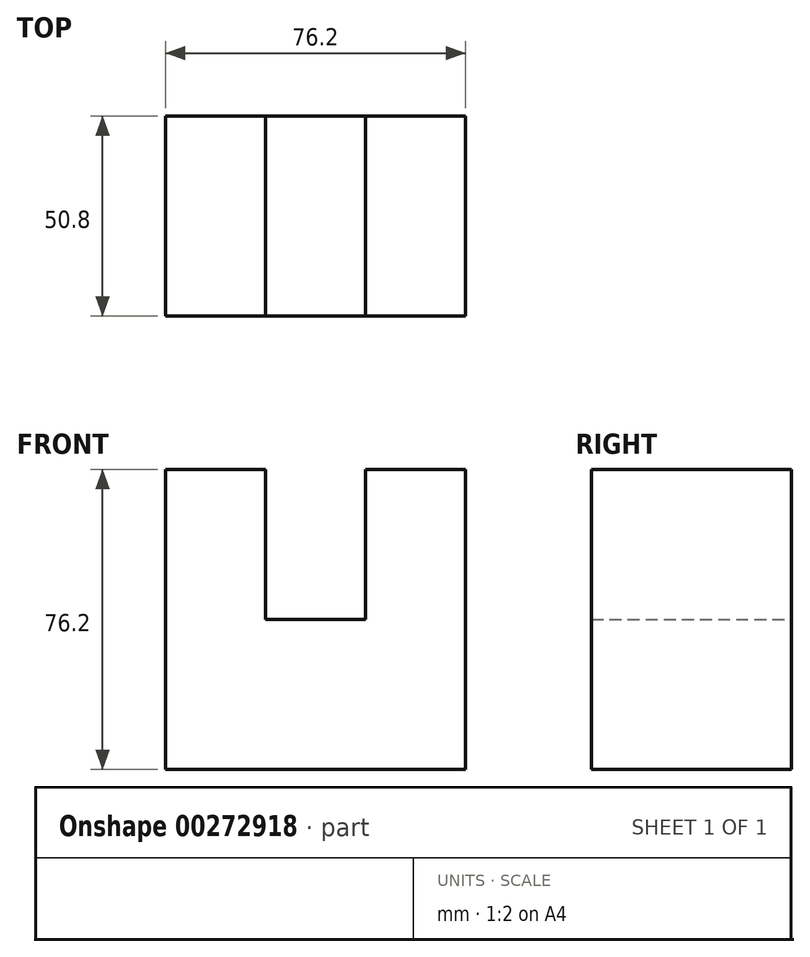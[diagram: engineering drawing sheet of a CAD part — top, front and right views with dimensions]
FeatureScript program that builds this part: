
annotation { "Feature Type Name" : "Feature", "Feature Type Description" : "" }
export const myFeature = defineFeature(function(context is Context, id is Id, definition is map)
    precondition{}
    {
        {
            var Q0;
            Q0=qCreatedBy(makeId("Front.planeOp"),FACE);
            var sketch = newSketch(context, id + "F0", { "sketchPlane" : qUnion([Q0])});
            skLineSegment(sketch, "E0", {"start": v(-67.41, 47.93) * mm, "end": v(-67.41, -28.27) * mm});
            skLineSegment(sketch, "E1", {"start": v(-67.41, -28.27) * mm, "end": v(8.79, -28.27) * mm});
            skLineSegment(sketch, "E2", {"start": v(8.79, -28.27) * mm, "end": v(8.79, 47.93) * mm});
            skLineSegment(sketch, "E3", {"start": v(-67.41, 47.93) * mm, "end": v(-42.01, 47.93) * mm});
            skLineSegment(sketch, "E4", {"start": v(-42.01, 47.93) * mm, "end": v(-42.01, 9.83) * mm});
            skLineSegment(sketch, "E5", {"start": v(-42.01, 9.83) * mm, "end": v(-16.61, 9.83) * mm});
            skLineSegment(sketch, "E6", {"start": v(-16.61, 9.83) * mm, "end": v(-16.61, 47.93) * mm});
            skLineSegment(sketch, "E7", {"start": v(-16.61, 47.93) * mm, "end": v(8.79, 47.93) * mm});
            skSolve(sketch);
        }
        {
            var Q0;
            Q0=makeQuery(id+"F0.imprint","IMPRINT",FACE,{"disambiguationData":[TD([[makeQuery(id+"F0.imprint","IMPRINT",EDGE,{"derivedFrom":sQuery(id+"F0.wireOp",EDGE,"E0")}),1.0]])]});
            extrude(context, id + "F1", {"entities" : qUnion([Q0]), "depth" : 50.8 * mm});
        }
    });
